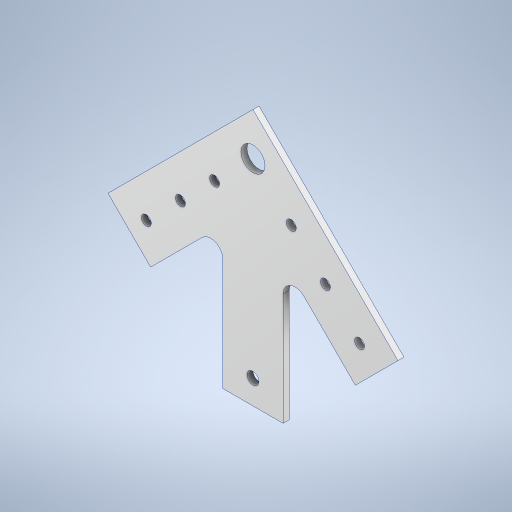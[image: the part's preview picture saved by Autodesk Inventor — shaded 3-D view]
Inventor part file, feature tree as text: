
AUTODESK INVENTOR PART (.ipt)
format: ipt  version: 2023 (Build 270158000, 158)  size: 293,376 bytes
history: native  units: mm
features: extrude x2, other x1, mirror x1, fillet x1, sketch x1, projected_geometry x1
ambient origin geometry x8: Origin, YZ Plane, XZ Plane, XY Plane, X Axis, Y Axis, Z Axis, Center Point
bodies: Solid1 (feature_tree)
feature tree (7):
  other  "<userpath>\OneDrive\Desktop\Robotics\URC Chassis Pivot\PivotParametersAndCalcs.xlsx"
  extrude  "Extrusion1"  Depth=3.175mm TaperAngle=0.0deg
  extrude  "Extrusion2"  Depth=6.35mm
  mirror  "Mirror1"
  fillet  "Fillet3"  Radius=12.7mm
  sketch  "Sketch2"  dims[d13=31.75mm d15=3.175mm d16=0.0mm d17=5.3mm d18=12.7mm d19=30.0mm d21=25.4mm d22=10.0mm d24=25.4mm d26=3.175mm d27=0.0mm d38=100.0mm d39=45.0deg d41=15.875mm d43=112.7mm d44=12.7mm d47=15.875mm d48=76.2mm d49=6.35mm]
  projected_geometry  "Projected Loop1"
